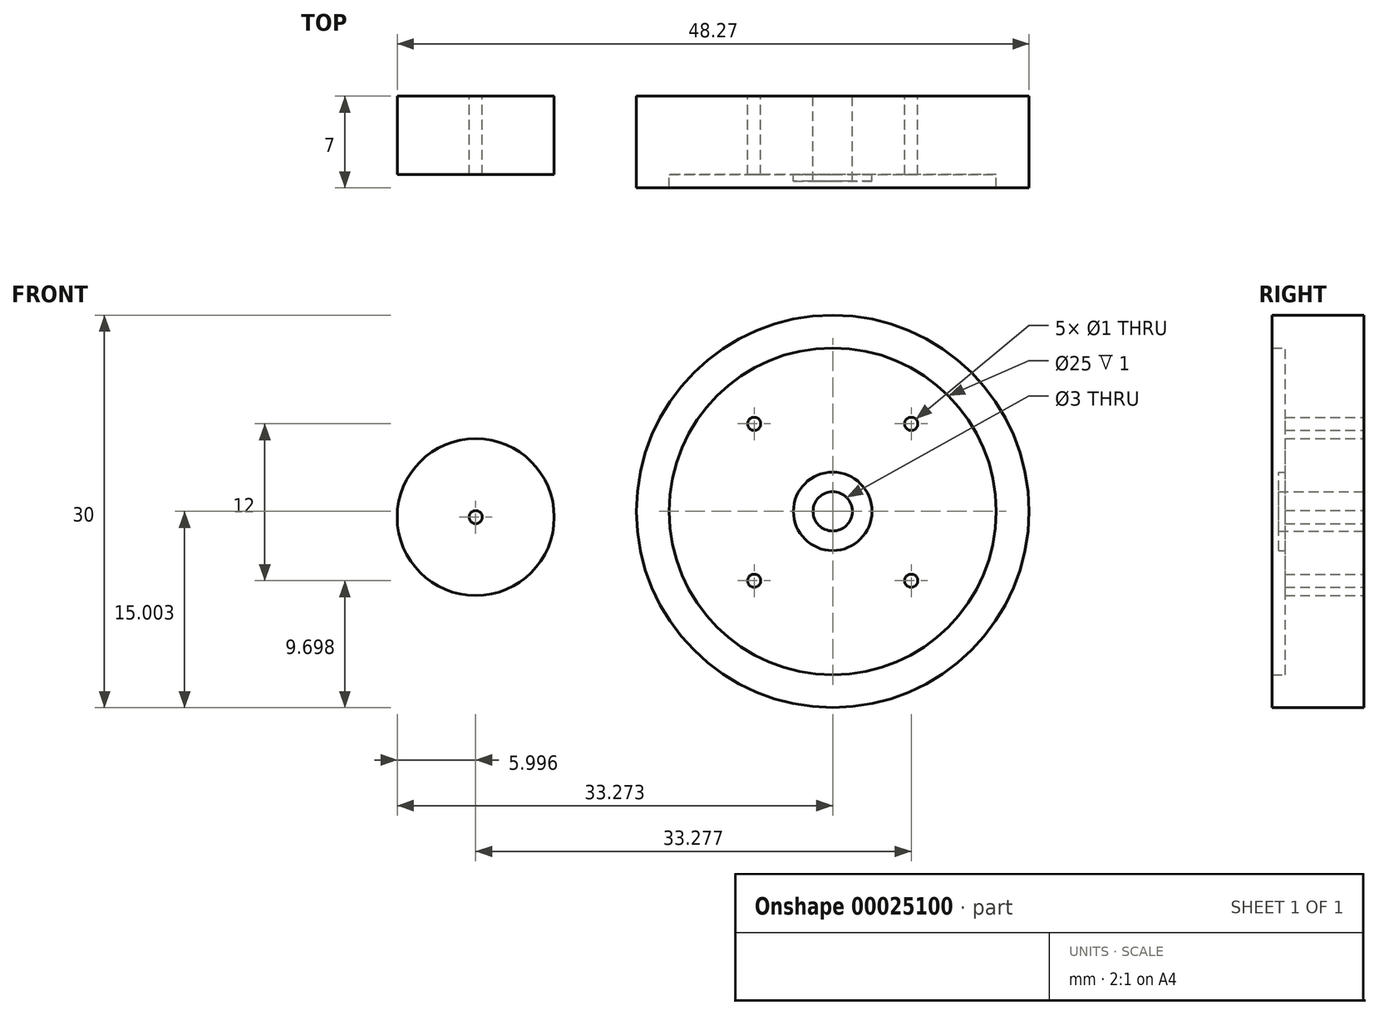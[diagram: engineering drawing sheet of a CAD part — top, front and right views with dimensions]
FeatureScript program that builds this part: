
annotation { "Feature Type Name" : "Feature", "Feature Type Description" : "" }
export const myFeature = defineFeature(function(context is Context, id is Id, definition is map)
    precondition{}
    {
        {
            var Q0;
            Q0=qCreatedBy(makeId("Front.planeOp"),FACE);
            var sketch = newSketch(context, id + "F0", { "sketchPlane" : qUnion([Q0])});
            skCircle(sketch, "E0", {"center": v(-47.93, 5.06) * mm, "radius": 15 * mm});
            skCircle(sketch, "E1", {"center": v(-47.93, 5.06) * mm, "radius": 12.5 * mm});
            skCircle(sketch, "E2", {"center": v(-47.93, 5.06) * mm, "radius": 1.5 * mm});
            skLineSegment(sketch, "E3.bottom", {"start": v(-53.93, -0.24) * mm, "end": v(-41.93, -0.24) * mm});
            skLineSegment(sketch, "E3.top", {"start": v(-53.93, 11.76) * mm, "end": v(-41.93, 11.76) * mm});
            skLineSegment(sketch, "E3.left", {"start": v(-53.93, -0.24) * mm, "end": v(-53.93, 11.76) * mm});
            skLineSegment(sketch, "E3.right", {"start": v(-41.93, -0.24) * mm, "end": v(-41.93, 11.76) * mm});
            skCircle(sketch, "E4", {"center": v(-53.93, 11.76) * mm, "radius": 0.5 * mm});
            skCircle(sketch, "E5", {"center": v(-41.93, 11.76) * mm, "radius": 0.5 * mm});
            skCircle(sketch, "E6", {"center": v(-41.93, -0.24) * mm, "radius": 0.5 * mm});
            skCircle(sketch, "E7", {"center": v(-53.93, -0.24) * mm, "radius": 0.5 * mm});
            skCircle(sketch, "E8", {"center": v(-47.93, 5.06) * mm, "radius": 3 * mm});
            skLineSegment(sketch, "E9", {"start": v(-47.93, 11.76) * mm, "end": v(-47.93, -0.24) * mm});
            skCircle(sketch, "E10", {"center": v(-75.2, 4.62) * mm, "radius": 0.5 * mm});
            skCircle(sketch, "E11", {"center": v(-75.2, 4.62) * mm, "radius": 6 * mm});
            skSolve(sketch);
        }
        {
            var Q0;
            Q0=makeQuery(id+"F0.imprint","IMPRINT",FACE,{"disambiguationData":[TD([[makeQuery(id+"F0.imprint","IMPRINT",EDGE,{"derivedFrom":sQuery(id+"F0.wireOp",EDGE,"E1")}),1.0]])]});
            var Q1;
            {var subQ3=sQuery(id+"F0.wireOp",EDGE,"E3.top");var subQ5=sQuery(id+"F0.wireOp",EDGE,"E4");var subQ7=makeQuery(id+"F0.imprint","INTERSECT",VERTEX,{"derivedFrom":[subQ3,subQ5]});Q1=makeQuery(id+"F0.imprint","IMPRINT",FACE,{"disambiguationData":[TD([[makeQuery(id+"F0.imprint","IMPRINT",EDGE,{"disambiguationData":[TD([[subQ7,-1.0]])],"derivedFrom":subQ3}),-1.0]])]});}
            var Q2;
            {var subQ0=sQuery(id+"F0.wireOp",EDGE,"E8");var subQ3=sQuery(id+"F0.wireOp",EDGE,"E3.top");var subQ4=makeQuery(id+"F0.imprint","INTERSECT",VERTEX,{"disambiguationData":[OD(1.0)],"derivedFrom":[subQ3,subQ0]});Q2=makeQuery(id+"F0.imprint","IMPRINT",FACE,{"disambiguationData":[TD([[makeQuery(id+"F0.imprint","IMPRINT",EDGE,{"disambiguationData":[TD([[subQ4,-1.0]])],"derivedFrom":subQ3}),-1.0]])]});}
            var Q3;
            {var subQ0=sQuery(id+"F0.wireOp",EDGE,"E8");var subQ3=sQuery(id+"F0.wireOp",EDGE,"E3.bottom");var subQ4=makeQuery(id+"F0.imprint","INTERSECT",VERTEX,{"disambiguationData":[OD(1.0)],"derivedFrom":[subQ3,subQ0]});Q3=makeQuery(id+"F0.imprint","IMPRINT",FACE,{"disambiguationData":[TD([[makeQuery(id+"F0.imprint","IMPRINT",EDGE,{"disambiguationData":[TD([[subQ4,-1.0]])],"derivedFrom":subQ3}),1.0]])]});}
            var Q4;
            {var subQ3=sQuery(id+"F0.wireOp",EDGE,"E3.bottom");var subQ5=sQuery(id+"F0.wireOp",EDGE,"E7");var subQ7=makeQuery(id+"F0.imprint","INTERSECT",VERTEX,{"derivedFrom":[subQ3,subQ5]});Q4=makeQuery(id+"F0.imprint","IMPRINT",FACE,{"disambiguationData":[TD([[makeQuery(id+"F0.imprint","IMPRINT",EDGE,{"disambiguationData":[TD([[subQ7,-1.0]])],"derivedFrom":subQ3}),1.0]])]});}
            var Q5;
            {var subQ0=sQuery(id+"F0.wireOp",EDGE,"E9");var subQ3=sQuery(id+"F0.wireOp",EDGE,"E3.bottom");var subQ4=makeQuery(id+"F0.imprint","INTERSECT",VERTEX,{"derivedFrom":[subQ3,subQ0]});Q5=makeQuery(id+"F0.imprint","IMPRINT",FACE,{"disambiguationData":[TD([[makeQuery(id+"F0.imprint","IMPRINT",EDGE,{"disambiguationData":[TD([[subQ4,-1.0]])],"derivedFrom":subQ3}),1.0]])]});}
            extrude(context, id + "F1", {"entities" : qUnion([Q0, Q1, Q2, Q3, Q4, Q5]), "depth" : 6 * mm});
        }
        {
            var Q0;
            Q0=makeQuery(id+"F0.imprint","IMPRINT",FACE,{"disambiguationData":[TD([[makeQuery(id+"F0.imprint","IMPRINT",EDGE,{"derivedFrom":sQuery(id+"F0.wireOp",EDGE,"E0")}),1.0]])]});
            extrude(context, id + "F2", {"entities" : qUnion([Q0]), "operationType" : NewBodyOperationType.ADD, "depth" : 7 * mm});
        }
        {
            var Q0;
            Q0=makeQuery(id+"F0.imprint","IMPRINT",FACE,{"disambiguationData":[TD([[makeQuery(id+"F0.imprint","IMPRINT",EDGE,{"derivedFrom":sQuery(id+"F0.wireOp",EDGE,"E2")}),-1.0]])]});
            var Q1;
            {var subQ0=sQuery(id+"F0.wireOp",EDGE,"E8");var subQ1=sQuery(id+"F0.wireOp",EDGE,"E3.left");var subQ3=makeQuery(id+"F0.imprint","INTERSECT",VERTEX,{"disambiguationData":[OD(0.0)],"derivedFrom":[subQ1,subQ0]});Q1=makeQuery(id+"F0.imprint","IMPRINT",FACE,{"disambiguationData":[TD([[makeQuery(id+"F0.imprint","IMPRINT",EDGE,{"disambiguationData":[TD([[subQ3,-1.0]])],"derivedFrom":subQ1}),1.0]])]});}
            var Q2;
            {var subQ0=sQuery(id+"F0.wireOp",EDGE,"E8");var subQ1=sQuery(id+"F0.wireOp",EDGE,"E3.top");var subQ3=makeQuery(id+"F0.imprint","INTERSECT",VERTEX,{"disambiguationData":[OD(0.0)],"derivedFrom":[subQ1,subQ0]});Q2=makeQuery(id+"F0.imprint","IMPRINT",FACE,{"disambiguationData":[TD([[makeQuery(id+"F0.imprint","IMPRINT",EDGE,{"disambiguationData":[TD([[subQ3,-1.0]])],"derivedFrom":subQ1}),1.0]])]});}
            var Q3;
            {var subQ0=sQuery(id+"F0.wireOp",EDGE,"E8");var subQ1=sQuery(id+"F0.wireOp",EDGE,"E3.right");var subQ3=makeQuery(id+"F0.imprint","INTERSECT",VERTEX,{"disambiguationData":[OD(0.0)],"derivedFrom":[subQ1,subQ0]});Q3=makeQuery(id+"F0.imprint","IMPRINT",FACE,{"disambiguationData":[TD([[makeQuery(id+"F0.imprint","IMPRINT",EDGE,{"disambiguationData":[TD([[subQ3,-1.0]])],"derivedFrom":subQ1}),-1.0]])]});}
            var Q4;
            {var subQ0=sQuery(id+"F0.wireOp",EDGE,"E8");var subQ1=sQuery(id+"F0.wireOp",EDGE,"E3.bottom");var subQ3=makeQuery(id+"F0.imprint","INTERSECT",VERTEX,{"disambiguationData":[OD(0.0)],"derivedFrom":[subQ1,subQ0]});Q4=makeQuery(id+"F0.imprint","IMPRINT",FACE,{"disambiguationData":[TD([[makeQuery(id+"F0.imprint","IMPRINT",EDGE,{"disambiguationData":[TD([[subQ3,-1.0]])],"derivedFrom":subQ1}),-1.0]])]});}
            extrude(context, id + "F3", {"entities" : qUnion([Q0, Q1, Q2, Q3, Q4]), "operationType" : NewBodyOperationType.ADD, "depth" : 6.5 * mm});
        }
        {
            var Q0;
            Q0=makeQuery(id+"F0.imprint","IMPRINT",FACE,{"disambiguationData":[TD([[makeQuery(id+"F0.imprint","IMPRINT",EDGE,{"derivedFrom":sQuery(id+"F0.wireOp",EDGE,"E10")}),-1.0]])]});
            extrude(context, id + "F4", {"entities" : qUnion([Q0]), "depth" : 6 * mm});
        }
    });
